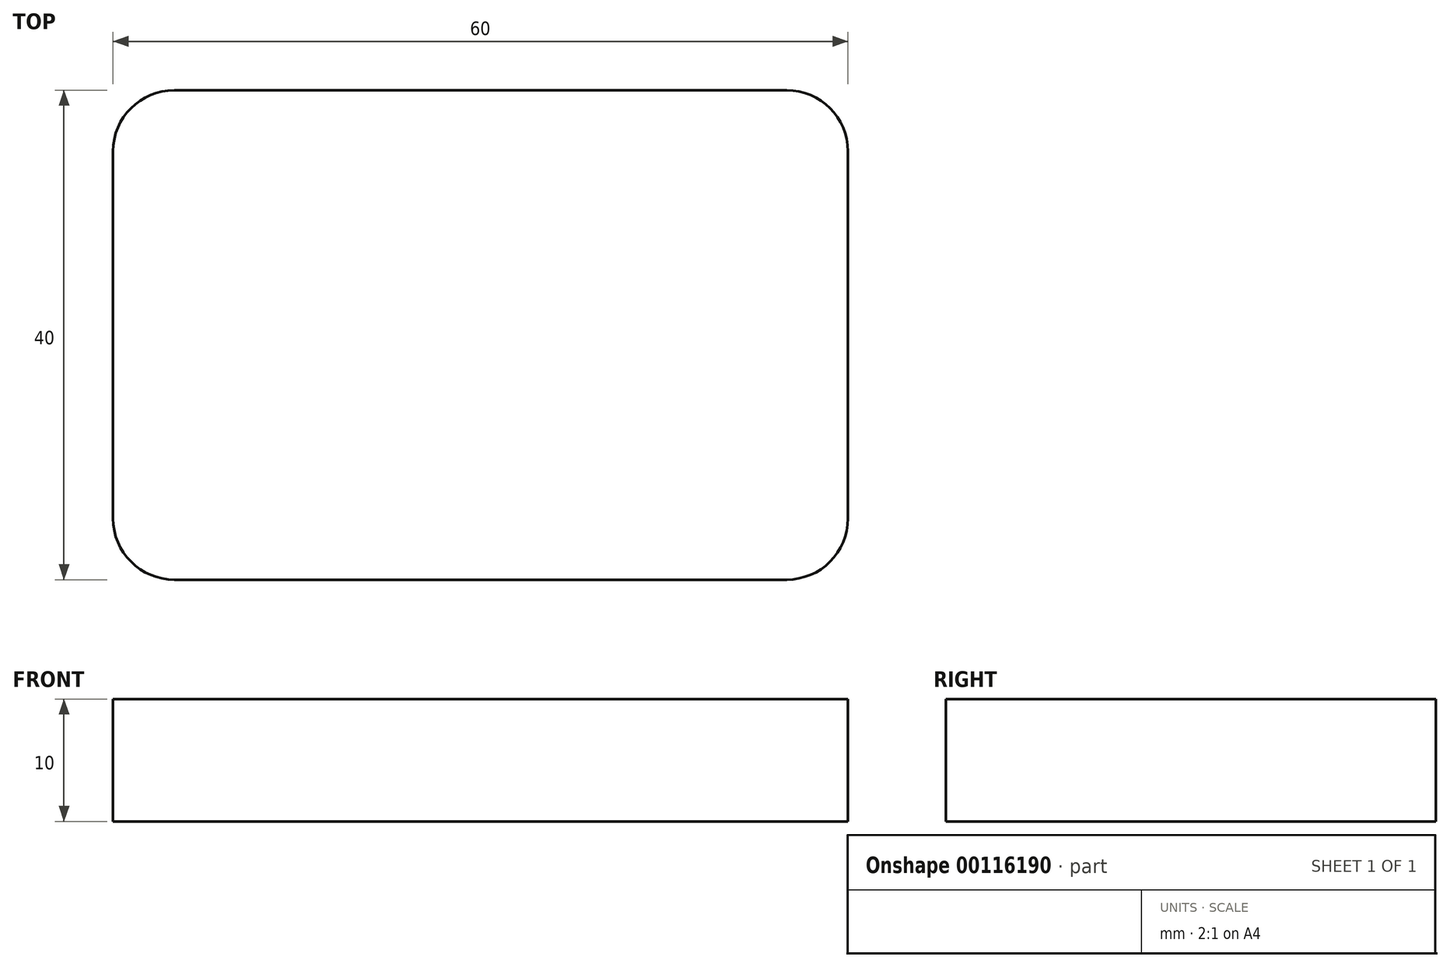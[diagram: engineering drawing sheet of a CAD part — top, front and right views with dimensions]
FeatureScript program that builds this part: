
annotation { "Feature Type Name" : "Feature", "Feature Type Description" : "" }
export const myFeature = defineFeature(function(context is Context, id is Id, definition is map)
    precondition{}
    {
        {
            var Q0;
            Q0=qCreatedBy(makeId("Top.planeOp"),FACE);
            var sketch = newSketch(context, id + "F0", { "sketchPlane" : qUnion([Q0])});
            skLineSegment(sketch, "E0.bottom", {"start": v(0, 0) * mm, "end": v(-60, 0) * mm});
            skLineSegment(sketch, "E0.top", {"start": v(0, 40) * mm, "end": v(-60, 40) * mm});
            skLineSegment(sketch, "E0.left", {"start": v(0, 0) * mm, "end": v(0, 40) * mm});
            skLineSegment(sketch, "E0.right", {"start": v(-60, 0) * mm, "end": v(-60, 40) * mm});
            skSolve(sketch);
        }
        {
            var Q0;
            Q0=makeQuery(id+"F0.imprint","IMPRINT",FACE,{"disambiguationData":[TD([[makeQuery(id+"F0.imprint","IMPRINT",EDGE,{"derivedFrom":sQuery(id+"F0.wireOp",EDGE,"E0.bottom")}),-1.0]])]});
            extrude(context, id + "F1", {"entities" : qUnion([Q0]), "depth" : 10 * mm});
        }
        {
            var Q0;
            Q0=makeQuery(id+"F1.opExtrude","SWEPT_EDGE",EDGE,{"disambiguationData":[OSD([sQuery(id+"F0.wireOp",EDGE,"E0.bottom"),sQuery(id+"F0.wireOp",EDGE,"E0.left")])]});
            var Q1;
            Q1=makeQuery(id+"F1.opExtrude","SWEPT_EDGE",EDGE,{"disambiguationData":[OSD([sQuery(id+"F0.wireOp",EDGE,"E0.top"),sQuery(id+"F0.wireOp",EDGE,"E0.left")])]});
            var Q2;
            Q2=makeQuery(id+"F1.opExtrude","SWEPT_EDGE",EDGE,{"disambiguationData":[OSD([sQuery(id+"F0.wireOp",EDGE,"E0.bottom"),sQuery(id+"F0.wireOp",EDGE,"E0.right")])]});
            var Q3;
            Q3=makeQuery(id+"F1.opExtrude","SWEPT_EDGE",EDGE,{"disambiguationData":[OSD([sQuery(id+"F0.wireOp",EDGE,"E0.top"),sQuery(id+"F0.wireOp",EDGE,"E0.right")])]});
            fillet(context, id + "F2", {"entities" : qUnion([Q0, Q1, Q2, Q3]), "radius" : 5 * mm, "tangentPropagation" : true, "allowEdgeOverflow" : false});
        }
    });
